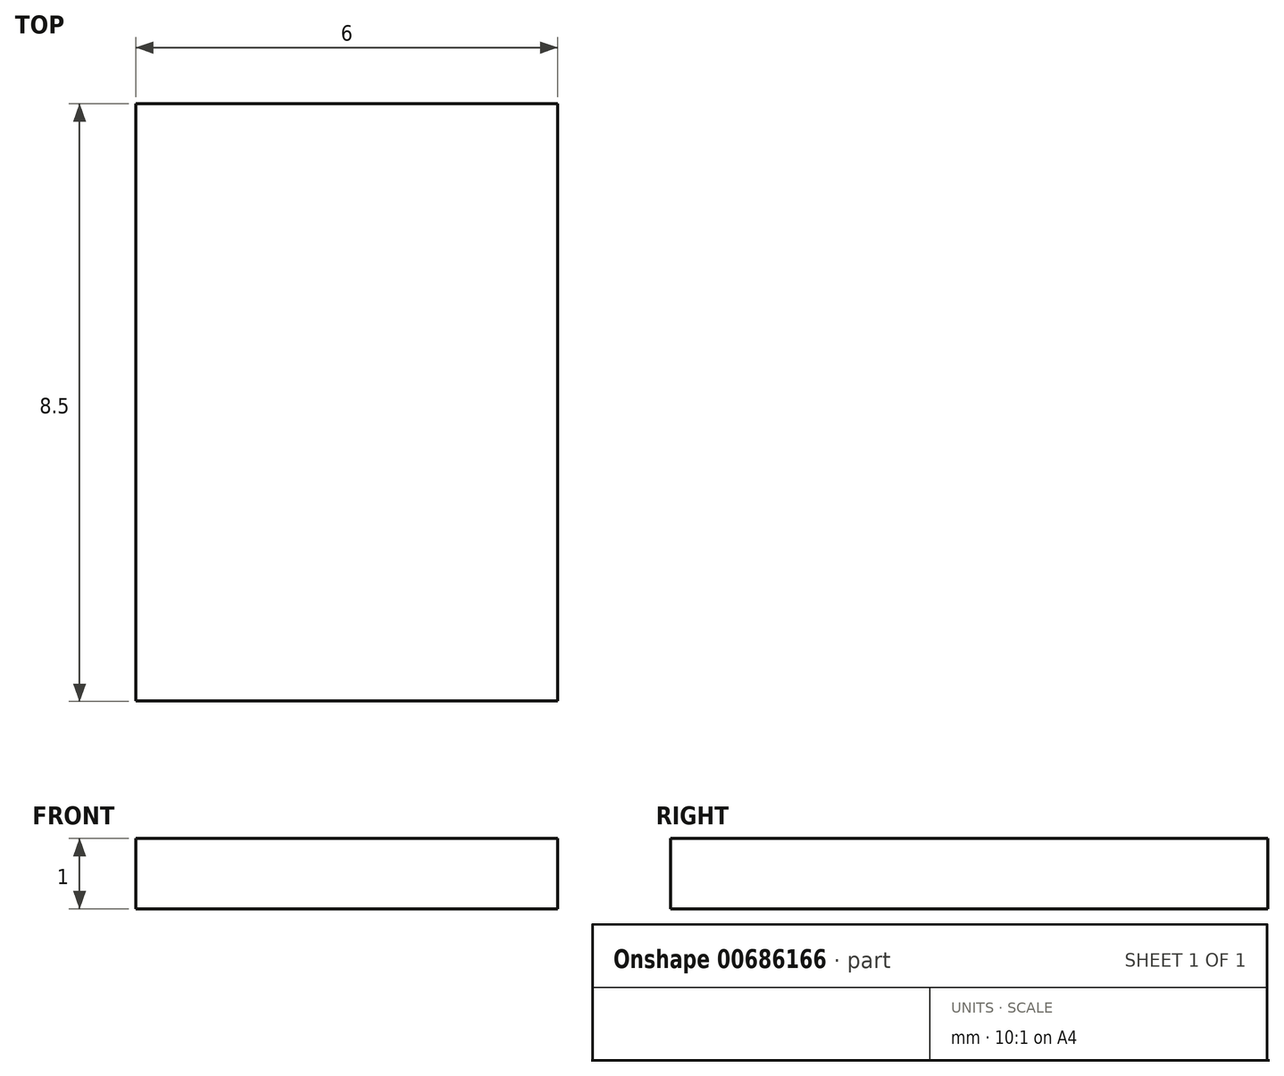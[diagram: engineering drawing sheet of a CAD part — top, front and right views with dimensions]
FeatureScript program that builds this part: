
annotation { "Feature Type Name" : "Feature", "Feature Type Description" : "" }
export const myFeature = defineFeature(function(context is Context, id is Id, definition is map)
    precondition{}
    {
        {
            var Q0;
            Q0=qCreatedBy(makeId("Top.planeOp"),FACE);
            var sketch = newSketch(context, id + "F0", { "sketchPlane" : qUnion([Q0])});
            skLineSegment(sketch, "E0.bottom", {"start": v(-4.44, 7.22) * mm, "end": v(1.56, 7.22) * mm});
            skLineSegment(sketch, "E0.top", {"start": v(-4.44, -1.28) * mm, "end": v(1.56, -1.28) * mm});
            skLineSegment(sketch, "E0.left", {"start": v(-4.44, 7.22) * mm, "end": v(-4.44, -1.28) * mm});
            skLineSegment(sketch, "E0.right", {"start": v(1.56, 7.22) * mm, "end": v(1.56, -1.28) * mm});
            skSolve(sketch);
        }
        {
            var Q0;
            Q0 = qSketchRegion(id + "F0", true);
            extrude(context, id + "F1", {"entities" : qUnion([Q0]), "depth" : 1 * mm, "offsetDistance" : 25.4 * mm});
        }
    });
